# Revit family: РИДАН_Клапан поворотный HFE-3R
name_source: partatom
category: Арматура трубопроводов
units: mm (PartAtom-declared; Revit-internal decimal feet)

## family parameters
Всегда вертикально = Да
На основе рабочей плоскости = Нет
Общий = Нет
При загрузке вырезать с полостями = Нет
Размер круглого соединителя = Использовать диаметр
Тип детали = Вставляется

## types (2) — shared parameters
ADSK_Версия Revit = 2019
ADSK_Версия семейства = 1.0
ADSK_Единица измерения = шт.
ADSK_Завод-изготовитель = ООО «Ридан-Трейд»
ADSK_Классификация нагрузок = Прочее
ADSK_Количество = 1
ADSK_Количество фаз = 1
ADSK_Коэффициент мощности = 1
ADSK_Потеря давления жидкости = 0.0 Па
ADSK_Расход жидкости = 0 м³/ч
LT = HFE-3R
LT_EL = Electro
URL = https://ridan.ru
a = 2 мм
n2 = 58 мм
o = 140 мм
p = 15 мм
r = 115 мм
Изготовитель = ООО «Ридан-Трейд»
Привод_AMB182R_1 = ► : AMB-182R-Имп,150 c,24 AC/DC,24
Привод_AMB182R_2 = ► : AMB-182R-Имп,150 c,230,230
Привод_AMB182R_3 = ► : AMB-182R-Ан,150 c,24 AC/DC,0(2)–10 В
Привод_Рукоятка = ► : Рукоятка
Расход_А = 0 м³/ч
Расход_В = 0 м³/ч

## per-type parameters (varying)
- DN 125: ADSK_Диаметр условный=125 мм; ADSK_Код изделия=065Z0436R; ADSK_Марка=HFE-3R DN125; ADSK_Масса=30.7; ADSK_Наименование=Клапан регулирующий поворотный HFE-3R фланцевый PN6, Tmax=110C, DN125, Kvs=280 м3\ч; ADSK_Пропускная способность=280 м³/ч; DN150=Нет; DN20_125=Да; b=17 мм; c=8 мм; d=126 мм; e=252 мм; f=163 мм; g=240 мм; h=184 мм; i=180 мм; j=158 мм; k=144 мм; l=146 мм; m=72 мм; n=84 мм; n1=84 мм; n3=83 мм; s=306 мм; s1=153 мм
- DN 150: ADSK_Диаметр условный=150 мм; ADSK_Код изделия=065Z0437R; ADSK_Марка=HFE-3R DN150; ADSK_Масса=40.4; ADSK_Наименование=Клапан регулирующий поворотный HFE-3R фланцевый PN6, Tmax=110C, DN150, Kvs=400 м3\ч; ADSK_Пропускная способность=400 м³/ч; DN150=Да; DN20_125=Нет; b=20 мм; c=91 мм; d=62 мм; e=125 мм; f=200 мм; g=265 мм; h=205 мм; i=201 мм; j=175 мм; k=128 мм; l=159 мм; m=78 мм; n=91 мм; n1=91 мм; n3=90 мм; s=350 мм; s1=175 мм
